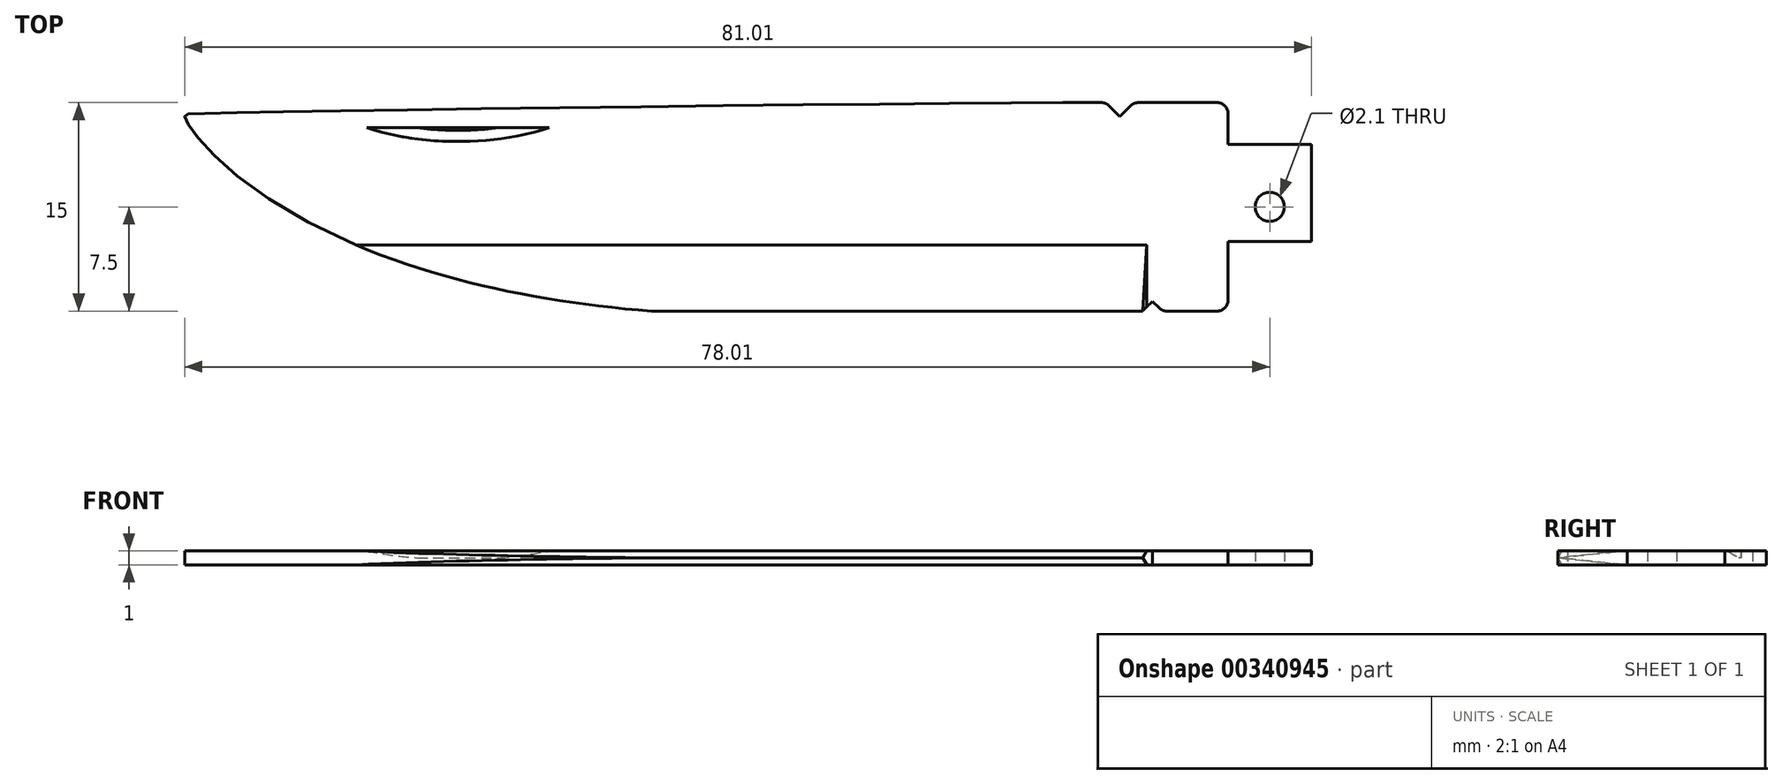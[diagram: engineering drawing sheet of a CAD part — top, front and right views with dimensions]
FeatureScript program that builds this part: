
annotation { "Feature Type Name" : "Feature", "Feature Type Description" : "" }
export const myFeature = defineFeature(function(context is Context, id is Id, definition is map)
    precondition{}
    {
        {
            var Q0;
            Q0=qCreatedBy(makeId("Top.planeOp"),FACE);
            var sketch = newSketch(context, id + "F0", { "sketchPlane" : qUnion([Q0])});
            skLineSegment(sketch, "E0", {"start": v(3, -2.5) * mm, "end": v(3, 4.5) * mm});
            skLineSegment(sketch, "E1", {"start": v(3, 4.5) * mm, "end": v(-3, 4.5) * mm});
            skLineSegment(sketch, "E2", {"start": v(-3, 4.5) * mm, "end": v(-3, 7.5) * mm});
            skLineSegment(sketch, "E3", {"start": v(-3, 7.5) * mm, "end": v(-9.78, 7.5) * mm});
            skLineSegment(sketch, "E4", {"start": v(-9.78, 7.5) * mm, "end": v(-10.78, 6.5) * mm});
            skLineSegment(sketch, "E5", {"start": v(-10.78, 6.5) * mm, "end": v(-11.78, 7.5) * mm});
            skLineSegment(sketch, "E6", {"start": v(3, -2.5) * mm, "end": v(-3, -2.5) * mm});
            skLineSegment(sketch, "E7", {"start": v(-3, -2.5) * mm, "end": v(-3, -7.5) * mm});
            skLineSegment(sketch, "E8", {"start": v(-3, -7.5) * mm, "end": v(-7.73, -7.5) * mm});
            skLineSegment(sketch, "E9", {"start": v(-9.13, -7.5) * mm, "end": v(-9.13, -7.5) * mm});
            skLineSegment(sketch, "E10", {"start": v(-9.13, -7.5) * mm, "end": v(-44.44, -7.5) * mm});
            skFitSpline(sketch, "E11", {"points": [v(-38.93, -7.78) * mm, v(-78, 6.5) * mm, v(-77.44, 6.7) * mm, v(-11.78, 7.5) * mm], "startDerivative": vector(-211.72, 5.2) * mm, "endDerivative": vector(58.87, -0.17) * mm});
            skLineSegment(sketch, "E12", {"start": v(-7.73, -7.5) * mm, "end": v(-8.43, -6.8) * mm});
            skLineSegment(sketch, "E13", {"start": v(-8.43, -6.8) * mm, "end": v(-9.13, -7.5) * mm});
            skCircle(sketch, "E14", {"center": v(0, 0) * mm, "radius": 1.05 * mm});
            skSolve(sketch);
        }
        {
            var Q0;
            Q0 = qSketchRegion(id + "F0", true);
            extrude(context, id + "F1", {"entities" : qUnion([Q0]), "endBound" : BoundingType.SYMMETRIC, "depth" : 1 * mm});
        }
        {
            var Q0;
            Q0=makeQuery(id+"F1.opExtrude","CAP_EDGE",EDGE,{"disambiguationData":[OSD([sQuery(id+"F0.wireOp",EDGE,"E10")])],"isStart":false});
            var Q1;
            Q1=makeQuery(id+"F1.opExtrude","CAP_EDGE",EDGE,{"disambiguationData":[OSD([sQuery(id+"F0.wireOp",EDGE,"E10")])],"isStart":true});
            chamfer(context, id + "F2", {"entities" : qUnion([Q0, Q1]), "chamferType" : ChamferType.OFFSET_ANGLE, "width" : .5 * mm, "oppositeDirection" : false, "angle" : 84 * degree, "tangentPropagation" : true});
        }
        {
            var Q0;
            Q0=makeQuery(id+"F1.opExtrude","CAP_EDGE",EDGE,{"disambiguationData":[OSD([sQuery(id+"F0.wireOp",EDGE,"E9")])],"isStart":false});
            chamfer(context, id + "F3", {"entities" : qUnion([Q0]), "chamferType" : ChamferType.OFFSET_ANGLE, "width" : .3 * mm, "oppositeDirection" : false, "angle" : 60 * degree, "tangentPropagation" : true});
        }
        {
            var Q0;
            Q0=makeQuery(id+"F1.opExtrude","CAP_EDGE",EDGE,{"disambiguationData":[OSD([sQuery(id+"F0.wireOp",EDGE,"E9")])],"isStart":true});
            chamfer(context, id + "F4", {"entities" : qUnion([Q0]), "chamferType" : ChamferType.OFFSET_ANGLE, "width" : .5 * mm, "oppositeDirection" : false, "angle" : 33 * degree, "tangentPropagation" : true});
        }
        {
            var Q0;
            Q0=makeQuery(id+"F1.opExtrude","SWEPT_EDGE",EDGE,{"disambiguationData":[OSD([sQuery(id+"F0.wireOp",EDGE,"E8"),sQuery(id+"F0.wireOp",EDGE,"E12")])]});
            var Q1;
            Q1=makeQuery(id+"F1.opExtrude","SWEPT_EDGE",EDGE,{"disambiguationData":[OSD([sQuery(id+"F0.wireOp",EDGE,"E3"),sQuery(id+"F0.wireOp",EDGE,"E4")])]});
            var Q2;
            Q2=makeQuery(id+"F1.opExtrude","SWEPT_EDGE",EDGE,{"disambiguationData":[OSD([sQuery(id+"F0.wireOp",EDGE,"E5"),sQuery(id+"F0.wireOp",EDGE,"E11")])]});
            var Q3;
            Q3=makeQuery(id+"F1.opExtrude","SWEPT_EDGE",EDGE,{"disambiguationData":[OSD([sQuery(id+"F0.wireOp",EDGE,"E2"),sQuery(id+"F0.wireOp",EDGE,"E3")])]});
            var Q4;
            Q4=makeQuery(id+"F1.opExtrude","SWEPT_EDGE",EDGE,{"disambiguationData":[OSD([sQuery(id+"F0.wireOp",EDGE,"E7"),sQuery(id+"F0.wireOp",EDGE,"E8")])]});
            fillet(context, id + "F5", {"entities" : qUnion([Q0, Q1, Q2, Q3, Q4]), "radius" : .8 * mm, "tangentPropagation" : true, "allowEdgeOverflow" : false});
        }
        {
            var Q0;
            Q0=makeQuery(id+"F1.opExtrude","CAP_FACE",FACE,{"disambiguationData":[OSD([sQuery(id+"F0.wireOp",EDGE,"E0"),sQuery(id+"F0.wireOp",EDGE,"E1"),sQuery(id+"F0.wireOp",EDGE,"E2"),sQuery(id+"F0.wireOp",EDGE,"E3"),sQuery(id+"F0.wireOp",EDGE,"E4"),sQuery(id+"F0.wireOp",EDGE,"E5"),sQuery(id+"F0.wireOp",EDGE,"E6"),sQuery(id+"F0.wireOp",EDGE,"E7"),sQuery(id+"F0.wireOp",EDGE,"E8"),sQuery(id+"F0.wireOp",EDGE,"E9"),sQuery(id+"F0.wireOp",EDGE,"E10"),sQuery(id+"F0.wireOp",EDGE,"E11"),sQuery(id+"F0.wireOp",EDGE,"E12"),sQuery(id+"F0.wireOp",EDGE,"E13"),sQuery(id+"F0.wireOp",EDGE,"E14")])],"isStart":false});
            var sketch = newSketch(context, id + "F6", { "sketchPlane" : qUnion([Q0])});
            skLineSegment(sketch, "E15", {"start": v(-64.92, 5.69) * mm, "end": v(-51.8, 5.69) * mm});
            skFitSpline(sketch, "E16", {"points": [v(-64.92, 5.69) * mm, v(-58.33, 4.7) * mm, v(-51.8, 5.69) * mm], "startDerivative": vector(12.94, -4.3) * mm, "endDerivative": vector(13.3, 4.28) * mm});
            skSolve(sketch);
        }
        {
            var Q0;
            Q0=makeQuery(id+"F6.imprint","IMPRINT",FACE,{"disambiguationData":[TD([[makeQuery(id+"F6.imprint","IMPRINT",EDGE,{"derivedFrom":sQuery(id+"F6.wireOp",EDGE,"E15")}),-1.0]])]});
            extrude(context, id + "F7", {"entities" : qUnion([Q0]), "operationType" : NewBodyOperationType.REMOVE, "oppositeDirection" : true, "depth" : .5 * mm});
        }
        {
            var Q0;
            Q0=makeQuery(id+"F7.boolean.opBoolean","COPY",EDGE,{"derivedFrom":makeQuery(id+"F7.opExtrude","CAP_EDGE",EDGE,{"disambiguationData":[OSD([sQuery(id+"F6.wireOp",EDGE,"E16")])],"isStart":false})});
            chamfer(context, id + "F8", {"entities" : qUnion([Q0]), "chamferType" : ChamferType.OFFSET_ANGLE, "width" : .8 * mm, "oppositeDirection" : false, "angle" : 31 * degree, "tangentPropagation" : true});
        }
    });
